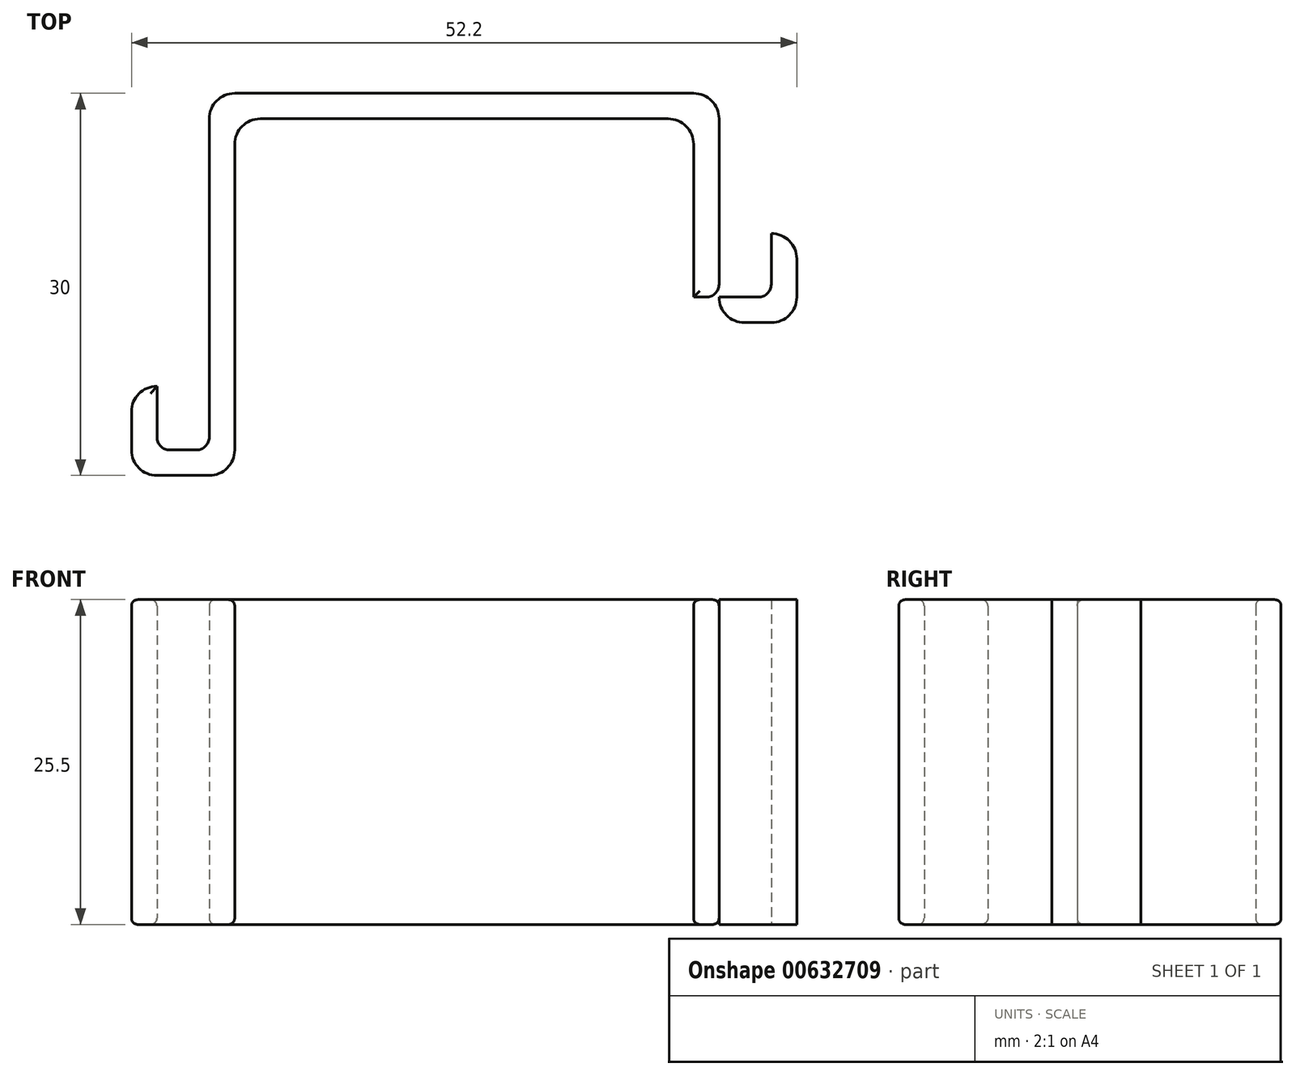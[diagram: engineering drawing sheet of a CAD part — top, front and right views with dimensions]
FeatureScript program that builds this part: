
annotation { "Feature Type Name" : "Feature", "Feature Type Description" : "" }
export const myFeature = defineFeature(function(context is Context, id is Id, definition is map)
    precondition{}
    {
        {
            var Q0;
            Q0=qCreatedBy(makeId("Top.planeOp"),FACE);
            var sketch = newSketch(context, id + "F0", { "sketchPlane" : qUnion([Q0])});
            skLineSegment(sketch, "E0.bottom", {"start": v(0, 0) * mm, "end": v(36, 0) * mm});
            skLineSegment(sketch, "E0.top", {"start": v(0, -2) * mm, "end": v(36, -2) * mm});
            skLineSegment(sketch, "E0.left", {"start": v(0, 0) * mm, "end": v(0, -2) * mm});
            skLineSegment(sketch, "E0.right", {"start": v(36, 0) * mm, "end": v(36, -2) * mm});
            skLineSegment(sketch, "E1.bottom", {"start": v(36, 0) * mm, "end": v(38, 0) * mm});
            skLineSegment(sketch, "E1.top", {"start": v(36, -18) * mm, "end": v(38, -18) * mm});
            skLineSegment(sketch, "E1.left", {"start": v(36, 0) * mm, "end": v(36, -18) * mm});
            skLineSegment(sketch, "E1.right", {"start": v(38, 0) * mm, "end": v(38, -18) * mm});
            skLineSegment(sketch, "E2.bottom", {"start": v(36, -18) * mm, "end": v(42.1, -18) * mm});
            skLineSegment(sketch, "E2.top", {"start": v(36, -16) * mm, "end": v(42.1, -16) * mm});
            skLineSegment(sketch, "E2.left", {"start": v(36, -16) * mm, "end": v(36, -18) * mm});
            skLineSegment(sketch, "E2.right", {"start": v(42.1, -16) * mm, "end": v(42.1, -18) * mm});
            skLineSegment(sketch, "E3.bottom", {"start": v(0, 0) * mm, "end": v(-2, 0) * mm});
            skLineSegment(sketch, "E3.top", {"start": v(0, -28) * mm, "end": v(-2, -28) * mm});
            skLineSegment(sketch, "E3.left", {"start": v(0, 0) * mm, "end": v(0, -28) * mm});
            skLineSegment(sketch, "E3.right", {"start": v(-2, 0) * mm, "end": v(-2, -28) * mm});
            skLineSegment(sketch, "E4.bottom", {"start": v(0, -28) * mm, "end": v(-6.1, -28) * mm});
            skLineSegment(sketch, "E4.top", {"start": v(0, -30) * mm, "end": v(-6.1, -30) * mm});
            skLineSegment(sketch, "E4.left", {"start": v(0, -28) * mm, "end": v(0, -30) * mm});
            skLineSegment(sketch, "E4.right", {"start": v(-6.1, -28) * mm, "end": v(-6.1, -30) * mm});
            skLineSegment(sketch, "E5.bottom", {"start": v(-6.1, -30) * mm, "end": v(-8.1, -30) * mm});
            skLineSegment(sketch, "E5.top", {"start": v(-6.1, -23) * mm, "end": v(-8.1, -23) * mm});
            skLineSegment(sketch, "E5.left", {"start": v(-6.1, -30) * mm, "end": v(-6.1, -23) * mm});
            skLineSegment(sketch, "E5.right", {"start": v(-8.1, -30) * mm, "end": v(-8.1, -23) * mm});
            skLineSegment(sketch, "E6.bottom", {"start": v(42.1, -18) * mm, "end": v(44.1, -18) * mm});
            skLineSegment(sketch, "E6.top", {"start": v(42.1, -11) * mm, "end": v(44.1, -11) * mm});
            skLineSegment(sketch, "E6.left", {"start": v(42.1, -18) * mm, "end": v(42.1, -11) * mm});
            skLineSegment(sketch, "E6.right", {"start": v(44.1, -18) * mm, "end": v(44.1, -11) * mm});
            skSolve(sketch);
        }
        {
            var Q0;
            {var subQ5=sQuery(id+"F0.wireOp",EDGE,"E3.bottom");Q0=makeQuery(id+"F0.imprint","IMPRINT",FACE,{"disambiguationData":[TD([[makeQuery(id+"F0.imprint","IMPRINT",EDGE,{"derivedFrom":subQ5}),1.0]])]});}
            var Q1;
            {var subQ0=sQuery(id+"F0.wireOp",EDGE,"E0.bottom");Q1=makeQuery(id+"F0.imprint","IMPRINT",FACE,{"disambiguationData":[TD([[makeQuery(id+"F0.imprint","IMPRINT",EDGE,{"derivedFrom":subQ0}),-1.0]])]});}
            var Q2;
            {var subQ1=sQuery(id+"F0.wireOp",EDGE,"E1.bottom");Q2=makeQuery(id+"F0.imprint","IMPRINT",FACE,{"disambiguationData":[TD([[makeQuery(id+"F0.imprint","IMPRINT",EDGE,{"derivedFrom":subQ1}),-1.0]])]});}
            var Q3;
            {var subQ5=sQuery(id+"F0.wireOp",EDGE,"E2.left");Q3=makeQuery(id+"F0.imprint","IMPRINT",FACE,{"disambiguationData":[TD([[makeQuery(id+"F0.imprint","IMPRINT",EDGE,{"derivedFrom":subQ5}),1.0]])]});}
            var Q4;
            {var subQ0=sQuery(id+"F0.wireOp",EDGE,"E2.bottom");var subQ1=sQuery(id+"F0.wireOp",EDGE,"E1.right");var subQ2=makeQuery(id+"F0.imprint","INTERSECT",VERTEX,{"derivedFrom":[subQ1,subQ0]});Q4=makeQuery(id+"F0.imprint","IMPRINT",FACE,{"disambiguationData":[TD([[makeQuery(id+"F0.imprint","IMPRINT",EDGE,{"disambiguationData":[TD([[subQ2,1.0]])],"derivedFrom":subQ1}),1.0]])]});}
            var Q5;
            {var subQ3=sQuery(id+"F0.wireOp",EDGE,"E6.bottom");Q5=makeQuery(id+"F0.imprint","IMPRINT",FACE,{"disambiguationData":[TD([[makeQuery(id+"F0.imprint","IMPRINT",EDGE,{"derivedFrom":subQ3}),1.0]])]});}
            var Q6;
            {var subQ1=sQuery(id+"F0.wireOp",EDGE,"E4.top");Q6=makeQuery(id+"F0.imprint","IMPRINT",FACE,{"disambiguationData":[TD([[makeQuery(id+"F0.imprint","IMPRINT",EDGE,{"derivedFrom":subQ1}),-1.0]])]});}
            var Q7;
            {var subQ3=sQuery(id+"F0.wireOp",EDGE,"E5.bottom");Q7=makeQuery(id+"F0.imprint","IMPRINT",FACE,{"disambiguationData":[TD([[makeQuery(id+"F0.imprint","IMPRINT",EDGE,{"derivedFrom":subQ3}),-1.0]])]});}
            extrude(context, id + "F1", {"entities" : qUnion([Q0, Q1, Q2, Q3, Q4, Q5, Q6, Q7]), "depth" : 25.5 * mm, "offsetDistance" : 25.4 * mm});
        }
        {
            var Q0;
            Q0=makeQuery(id+"F1.opExtrude","SWEPT_EDGE",EDGE,{"disambiguationData":[OSD([sQuery(id+"F0.wireOp",EDGE,"E4.top"),sQuery(id+"F0.wireOp",EDGE,"E4.left")])]});
            var Q1;
            Q1=makeQuery(id+"F1.opExtrude","SWEPT_EDGE",EDGE,{"disambiguationData":[OSD([sQuery(id+"F0.wireOp",EDGE,"E2.bottom"),sQuery(id+"F0.wireOp",EDGE,"E2.left")])]});
            var Q2;
            Q2=makeQuery(id+"F1.opExtrude","SWEPT_EDGE",EDGE,{"disambiguationData":[OSD([sQuery(id+"F0.wireOp",EDGE,"E5.bottom"),sQuery(id+"F0.wireOp",EDGE,"E5.right")])]});
            var Q3;
            Q3=makeQuery(id+"F1.opExtrude","SWEPT_EDGE",EDGE,{"disambiguationData":[OSD([sQuery(id+"F0.wireOp",EDGE,"E6.bottom"),sQuery(id+"F0.wireOp",EDGE,"E6.right")])]});
            var Q4;
            Q4=makeQuery(id+"F1.opExtrude","SWEPT_EDGE",EDGE,{"disambiguationData":[OSD([sQuery(id+"F0.wireOp",EDGE,"E0.top"),sQuery(id+"F0.wireOp",EDGE,"E3.left")])]});
            var Q5;
            Q5=makeQuery(id+"F1.opExtrude","SWEPT_EDGE",EDGE,{"disambiguationData":[OSD([sQuery(id+"F0.wireOp",EDGE,"E0.top"),sQuery(id+"F0.wireOp",EDGE,"E1.left")])]});
            var Q6;
            Q6=makeQuery(id+"F1.opExtrude","SWEPT_EDGE",EDGE,{"disambiguationData":[OSD([sQuery(id+"F0.wireOp",EDGE,"E3.bottom"),sQuery(id+"F0.wireOp",EDGE,"E3.right")])]});
            var Q7;
            Q7=makeQuery(id+"F1.opExtrude","SWEPT_EDGE",EDGE,{"disambiguationData":[OSD([sQuery(id+"F0.wireOp",EDGE,"E1.bottom"),sQuery(id+"F0.wireOp",EDGE,"E1.right")])]});
            var Q8;
            Q8=makeQuery(id+"F1.opExtrude","SWEPT_EDGE",EDGE,{"disambiguationData":[OSD([sQuery(id+"F0.wireOp",EDGE,"E6.top"),sQuery(id+"F0.wireOp",EDGE,"E6.right")])]});
            var Q9;
            Q9=makeQuery(id+"F1.opExtrude","SWEPT_EDGE",EDGE,{"disambiguationData":[OSD([sQuery(id+"F0.wireOp",EDGE,"E5.top"),sQuery(id+"F0.wireOp",EDGE,"E5.right")])]});
            fillet(context, id + "F2", {"entities" : qUnion([Q0, Q1, Q2, Q3, Q4, Q5, Q6, Q7, Q8, Q9]), "radius" : 2 * mm, "tangentPropagation" : true, "allowEdgeOverflow" : false});
        }
        {
            var Q0;
            Q0=makeQuery(id+"F1.opExtrude","SWEPT_EDGE",EDGE,{"disambiguationData":[OSD([sQuery(id+"F0.wireOp",EDGE,"E3.right"),sQuery(id+"F0.wireOp",EDGE,"E4.bottom")])]});
            var Q1;
            Q1=makeQuery(id+"F1.opExtrude","SWEPT_EDGE",EDGE,{"disambiguationData":[OSD([sQuery(id+"F0.wireOp",EDGE,"E4.bottom"),sQuery(id+"F0.wireOp",EDGE,"E5.left")])]});
            var Q2;
            Q2=makeQuery(id+"F1.opExtrude","SWEPT_EDGE",EDGE,{"disambiguationData":[OSD([sQuery(id+"F0.wireOp",EDGE,"E2.top"),sQuery(id+"F0.wireOp",EDGE,"E6.left")])]});
            var Q3;
            Q3=makeQuery(id+"F1.opExtrude","SWEPT_EDGE",EDGE,{"disambiguationData":[OSD([sQuery(id+"F0.wireOp",EDGE,"E1.right"),sQuery(id+"F0.wireOp",EDGE,"E2.top")])]});
            fillet(context, id + "F3", {"entities" : qUnion([Q0, Q1, Q2, Q3]), "radius" : 1 * mm, "tangentPropagation" : true, "allowEdgeOverflow" : false});
        }
        {
            var Q0;
            Q0=makeQuery(id+"F1.opExtrude","CAP_EDGE",EDGE,{"disambiguationData":[OSD([sQuery(id+"F0.wireOp",EDGE,"E0.bottom"),sQuery(id+"F0.wireOp",EDGE,"E1.bottom"),sQuery(id+"F0.wireOp",EDGE,"E3.bottom")])],"isStart":false});
            var Q1;
            Q1=makeQuery(id+"F1.opExtrude","CAP_EDGE",EDGE,{"disambiguationData":[OSD([sQuery(id+"F0.wireOp",EDGE,"E0.bottom"),sQuery(id+"F0.wireOp",EDGE,"E1.bottom"),sQuery(id+"F0.wireOp",EDGE,"E3.bottom")])],"isStart":true});
            var Q2;
            Q2=makeQuery(id+"F1.opExtrude","CAP_EDGE",EDGE,{"disambiguationData":[OSD([sQuery(id+"F0.wireOp",EDGE,"E0.top")])],"isStart":true});
            var Q3;
            Q3=makeQuery(id+"F1.opExtrude","CAP_FACE",FACE,{"disambiguationData":[OSD([sQuery(id+"F0.wireOp",EDGE,"E0.bottom"),sQuery(id+"F0.wireOp",EDGE,"E0.top"),sQuery(id+"F0.wireOp",EDGE,"E1.bottom"),sQuery(id+"F0.wireOp",EDGE,"E1.left"),sQuery(id+"F0.wireOp",EDGE,"E1.right"),sQuery(id+"F0.wireOp",EDGE,"E2.bottom"),sQuery(id+"F0.wireOp",EDGE,"E2.top"),sQuery(id+"F0.wireOp",EDGE,"E2.left"),sQuery(id+"F0.wireOp",EDGE,"E3.bottom"),sQuery(id+"F0.wireOp",EDGE,"E3.left"),sQuery(id+"F0.wireOp",EDGE,"E3.right"),sQuery(id+"F0.wireOp",EDGE,"E4.bottom"),sQuery(id+"F0.wireOp",EDGE,"E4.top"),sQuery(id+"F0.wireOp",EDGE,"E4.left"),sQuery(id+"F0.wireOp",EDGE,"E5.bottom"),sQuery(id+"F0.wireOp",EDGE,"E5.top"),sQuery(id+"F0.wireOp",EDGE,"E5.left"),sQuery(id+"F0.wireOp",EDGE,"E5.right"),sQuery(id+"F0.wireOp",EDGE,"E6.bottom"),sQuery(id+"F0.wireOp",EDGE,"E6.top"),sQuery(id+"F0.wireOp",EDGE,"E6.left"),sQuery(id+"F0.wireOp",EDGE,"E6.right")])],"isStart":false});
            fillet(context, id + "F4", {"entities" : qUnion([Q0, Q1, Q2, Q3]), "radius" : 0.5 * mm, "tangentPropagation" : true, "allowEdgeOverflow" : false});
        }
    });
